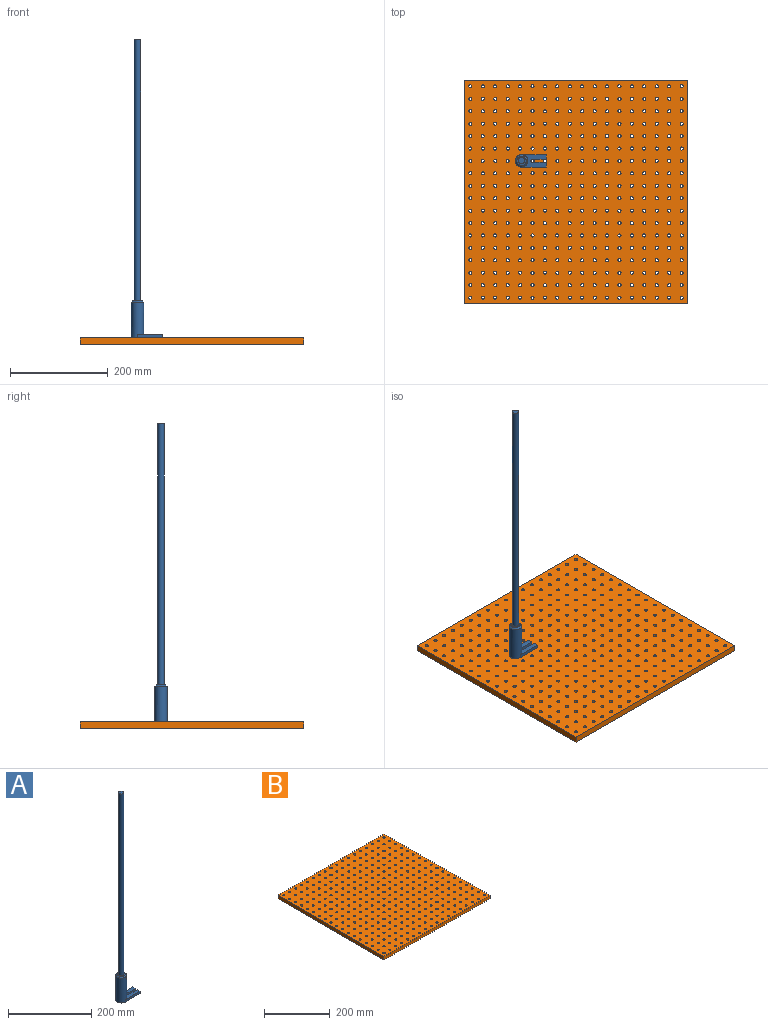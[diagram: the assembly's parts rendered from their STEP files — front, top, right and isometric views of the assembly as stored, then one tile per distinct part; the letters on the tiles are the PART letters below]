
ASSEMBLY  parts=2 mates=1
PART A: 14 faces, bbox 63.8x25.4x609.6 mm
  f0: cylinder r=12.7mm len=73.03mm, axis (0,0,-1), area 5575.7mm2, adj f2,f3,f7,f8,f11
  f1: plane 19.05x19.05mm, normal (0,0,1), area 158.3mm2, adj f11,f12
  f2: plane 63.8x25.4mm, normal (0,0,-1), area 1351mm2, adj f0,f4,f5,f6,f7,f8,f9,f10
  f3: plane 51.1x25.4mm, normal (0,0,1), area 844.3mm2, adj f0,f4,f5,f6,f7,f8,f9,f10
  f4: cylinder r=3.17mm len=6.35mm, axis (0,0,-1), area 62.4mm2, adj f2,f3,f5,f10
  f5: plane 28.58x6.35mm, normal (0,1,0), area 181.5mm2, adj f2,f3,f4,f6
  f6: plane 9.53x6.35mm, normal (1,0,0), area 60.5mm2, adj f2,f3,f5,f7
  f7: plane 50.8x6.35mm, normal (0,-1,0), area 322.6mm2, adj f0,f2,f3,f6
  f8: plane 50.8x6.35mm, normal (0,1,0), area 322.6mm2, adj f0,f2,f3,f9
  f9: plane 9.53x6.35mm, normal (1,0,0), area 60.5mm2, adj f2,f3,f8,f10
  f10: plane 28.43x6.35mm, normal (0,-1,0), area 180.5mm2, adj f2,f3,f4,f9
  f11: cone r=9.53mm half-angle=45deg, axis (0,0,-1), area 313.5mm2, adj f0,f1
  f12: cylinder r=6.35mm len=533.4mm, axis (0,0,-1), area 21281.7mm2, adj f1,f13
  f13: plane 12.7x12.7mm, normal (0,0,1), area 126.7mm2, adj f12
PART B: 330 faces, bbox 457.2x457.2x12.7 mm
  f0: plane 457.2x12.7mm, normal (-1,0,0), area 5806.4mm2, adj f1,f326,f328,f329
  f1: plane 457.2x12.7mm, normal (0,-1,0), area 5806.4mm2, adj f0,f2,f328,f329
  f2: plane 457.2x12.7mm, normal (1,0,0), area 5806.4mm2, adj f1,f326,f328,f329
  f3: cylinder r=3.17mm len=12.7mm, axis (0,0,-1), area 253.4mm2, adj f328,f329
  f4: cylinder r=3.17mm len=12.7mm, axis (0,0,-1), area 253.4mm2, adj f328,f329
  f5: cylinder r=3.17mm len=12.7mm, axis (0,0,-1), area 253.4mm2, adj f328,f329
  f6: cylinder r=3.17mm len=12.7mm, axis (0,0,-1), area 253.4mm2, adj f328,f329
  f7: cylinder r=3.17mm len=12.7mm, axis (0,0,-1), area 253.4mm2, adj f328,f329
  f8: cylinder r=3.17mm len=12.7mm, axis (0,0,-1), area 253.4mm2, adj f328,f329
  f9: cylinder r=3.17mm len=12.7mm, axis (0,0,-1), area 253.4mm2, adj f328,f329
  f10: cylinder r=3.17mm len=12.7mm, axis (0,0,-1), area 253.4mm2, adj f328,f329
  f11: cylinder r=3.17mm len=12.7mm, axis (0,0,-1), area 253.4mm2, adj f328,f329
  f12: cylinder r=3.17mm len=12.7mm, axis (0,0,-1), area 253.4mm2, adj f328,f329
  f13: cylinder r=3.17mm len=12.7mm, axis (0,0,-1), area 253.4mm2, adj f328,f329
  f14: cylinder r=3.17mm len=12.7mm, axis (0,0,-1), area 253.4mm2, adj f328,f329
  f15: cylinder r=3.17mm len=12.7mm, axis (0,0,-1), area 253.4mm2, adj f328,f329
  f16: cylinder r=3.17mm len=12.7mm, axis (0,0,-1), area 253.4mm2, adj f328,f329
  f17: cylinder r=3.17mm len=12.7mm, axis (0,0,-1), area 253.4mm2, adj f328,f329
  f18: cylinder r=3.17mm len=12.7mm, axis (0,0,-1), area 253.4mm2, adj f328,f329
  f19: cylinder r=3.17mm len=12.7mm, axis (0,0,-1), area 253.4mm2, adj f328,f329
  f20: cylinder r=3.17mm len=12.7mm, axis (0,0,-1), area 253.4mm2, adj f328,f329
  f21: cylinder r=3.17mm len=12.7mm, axis (0,0,-1), area 253.4mm2, adj f328,f329
  f22: cylinder r=3.17mm len=12.7mm, axis (0,0,-1), area 253.4mm2, adj f328,f329
  f23: cylinder r=3.17mm len=12.7mm, axis (0,0,-1), area 253.4mm2, adj f328,f329
  f24: cylinder r=3.17mm len=12.7mm, axis (0,0,-1), area 253.4mm2, adj f328,f329
  f25: cylinder r=3.17mm len=12.7mm, axis (0,0,-1), area 253.4mm2, adj f328,f329
  f26: cylinder r=3.17mm len=12.7mm, axis (0,0,-1), area 253.4mm2, adj f328,f329
  f27: cylinder r=3.17mm len=12.7mm, axis (0,0,-1), area 253.4mm2, adj f328,f329
  f28: cylinder r=3.17mm len=12.7mm, axis (0,0,-1), area 253.4mm2, adj f328,f329
  f29: cylinder r=3.17mm len=12.7mm, axis (0,0,-1), area 253.4mm2, adj f328,f329
  f30: cylinder r=3.17mm len=12.7mm, axis (0,0,-1), area 253.4mm2, adj f328,f329
  f31: cylinder r=3.17mm len=12.7mm, axis (0,0,-1), area 253.4mm2, adj f328,f329
  f32: cylinder r=3.17mm len=12.7mm, axis (0,0,-1), area 253.4mm2, adj f328,f329
  f33: cylinder r=3.17mm len=12.7mm, axis (0,0,-1), area 253.4mm2, adj f328,f329
  f34: cylinder r=3.17mm len=12.7mm, axis (0,0,-1), area 253.4mm2, adj f328,f329
  f35: cylinder r=3.17mm len=12.7mm, axis (0,0,-1), area 253.4mm2, adj f328,f329
  f36: cylinder r=3.17mm len=12.7mm, axis (0,0,-1), area 253.4mm2, adj f328,f329
  f37: cylinder r=3.17mm len=12.7mm, axis (0,0,-1), area 253.4mm2, adj f328,f329
  f38: cylinder r=3.17mm len=12.7mm, axis (0,0,-1), area 253.4mm2, adj f328,f329
  f39: cylinder r=3.17mm len=12.7mm, axis (0,0,-1), area 253.4mm2, adj f328,f329
  f40: cylinder r=3.17mm len=12.7mm, axis (0,0,-1), area 253.4mm2, adj f328,f329
  f41: cylinder r=3.17mm len=12.7mm, axis (0,0,-1), area 253.4mm2, adj f328,f329
  f42: cylinder r=3.17mm len=12.7mm, axis (0,0,-1), area 253.4mm2, adj f328,f329
  f43: cylinder r=3.17mm len=12.7mm, axis (0,0,-1), area 253.4mm2, adj f328,f329
  f44: cylinder r=3.17mm len=12.7mm, axis (0,0,-1), area 253.4mm2, adj f328,f329
  f45: cylinder r=3.17mm len=12.7mm, axis (0,0,-1), area 253.4mm2, adj f328,f329
  f46: cylinder r=3.17mm len=12.7mm, axis (0,0,-1), area 253.4mm2, adj f328,f329
  f47: cylinder r=3.17mm len=12.7mm, axis (0,0,-1), area 253.4mm2, adj f328,f329
  f48: cylinder r=3.17mm len=12.7mm, axis (0,0,-1), area 253.4mm2, adj f328,f329
  f49: cylinder r=3.17mm len=12.7mm, axis (0,0,-1), area 253.4mm2, adj f328,f329
  f50: cylinder r=3.17mm len=12.7mm, axis (0,0,-1), area 253.4mm2, adj f328,f329
  f51: cylinder r=3.17mm len=12.7mm, axis (0,0,-1), area 253.4mm2, adj f328,f329
  f52: cylinder r=3.17mm len=12.7mm, axis (0,0,-1), area 253.4mm2, adj f328,f329
  f53: cylinder r=3.17mm len=12.7mm, axis (0,0,-1), area 253.4mm2, adj f328,f329
  f54: cylinder r=3.17mm len=12.7mm, axis (0,0,-1), area 253.4mm2, adj f328,f329
  f55: cylinder r=3.17mm len=12.7mm, axis (0,0,-1), area 253.4mm2, adj f328,f329
  f56: cylinder r=3.17mm len=12.7mm, axis (0,0,-1), area 253.4mm2, adj f328,f329
  f57: cylinder r=3.17mm len=12.7mm, axis (0,0,-1), area 253.4mm2, adj f328,f329
  f58: cylinder r=3.17mm len=12.7mm, axis (0,0,-1), area 253.4mm2, adj f328,f329
  f59: cylinder r=3.17mm len=12.7mm, axis (0,0,-1), area 253.4mm2, adj f328,f329
  f60: cylinder r=3.17mm len=12.7mm, axis (0,0,-1), area 253.4mm2, adj f328,f329
  f61: cylinder r=3.17mm len=12.7mm, axis (0,0,-1), area 253.4mm2, adj f328,f329
  f62: cylinder r=3.17mm len=12.7mm, axis (0,0,-1), area 253.4mm2, adj f328,f329
  f63: cylinder r=3.17mm len=12.7mm, axis (0,0,-1), area 253.4mm2, adj f328,f329
  f64: cylinder r=3.17mm len=12.7mm, axis (0,0,-1), area 253.4mm2, adj f328,f329
  f65: cylinder r=3.17mm len=12.7mm, axis (0,0,-1), area 253.4mm2, adj f328,f329
  f66: cylinder r=3.17mm len=12.7mm, axis (0,0,-1), area 253.4mm2, adj f328,f329
  f67: cylinder r=3.17mm len=12.7mm, axis (0,0,-1), area 253.4mm2, adj f328,f329
  f68: cylinder r=3.17mm len=12.7mm, axis (0,0,-1), area 253.4mm2, adj f328,f329
  f69: cylinder r=3.17mm len=12.7mm, axis (0,0,-1), area 253.4mm2, adj f328,f329
  f70: cylinder r=3.17mm len=12.7mm, axis (0,0,-1), area 253.4mm2, adj f328,f329
  f71: cylinder r=3.17mm len=12.7mm, axis (0,0,-1), area 253.4mm2, adj f328,f329
  f72: cylinder r=3.17mm len=12.7mm, axis (0,0,-1), area 253.4mm2, adj f328,f329
  f73: cylinder r=3.17mm len=12.7mm, axis (0,0,-1), area 253.4mm2, adj f328,f329
  f74: cylinder r=3.17mm len=12.7mm, axis (0,0,-1), area 253.4mm2, adj f328,f329
  f75: cylinder r=3.17mm len=12.7mm, axis (0,0,-1), area 253.4mm2, adj f328,f329
  f76: cylinder r=3.17mm len=12.7mm, axis (0,0,-1), area 253.4mm2, adj f328,f329
  f77: cylinder r=3.17mm len=12.7mm, axis (0,0,-1), area 253.4mm2, adj f328,f329
  f78: cylinder r=3.17mm len=12.7mm, axis (0,0,-1), area 253.4mm2, adj f328,f329
  f79: cylinder r=3.17mm len=12.7mm, axis (0,0,-1), area 253.4mm2, adj f328,f329
  f80: cylinder r=3.17mm len=12.7mm, axis (0,0,-1), area 253.4mm2, adj f328,f329
  f81: cylinder r=3.17mm len=12.7mm, axis (0,0,-1), area 253.4mm2, adj f328,f329
  f82: cylinder r=3.17mm len=12.7mm, axis (0,0,-1), area 253.4mm2, adj f328,f329
  f83: cylinder r=3.17mm len=12.7mm, axis (0,0,-1), area 253.4mm2, adj f328,f329
  f84: cylinder r=3.17mm len=12.7mm, axis (0,0,-1), area 253.4mm2, adj f328,f329
  f85: cylinder r=3.17mm len=12.7mm, axis (0,0,-1), area 253.4mm2, adj f328,f329
  f86: cylinder r=3.17mm len=12.7mm, axis (0,0,-1), area 253.4mm2, adj f328,f329
  f87: cylinder r=3.17mm len=12.7mm, axis (0,0,-1), area 253.4mm2, adj f328,f329
  f88: cylinder r=3.17mm len=12.7mm, axis (0,0,-1), area 253.4mm2, adj f328,f329
  f89: cylinder r=3.17mm len=12.7mm, axis (0,0,-1), area 253.4mm2, adj f328,f329
  f90: cylinder r=3.17mm len=12.7mm, axis (0,0,-1), area 253.4mm2, adj f328,f329
  f91: cylinder r=3.17mm len=12.7mm, axis (0,0,-1), area 253.4mm2, adj f328,f329
  f92: cylinder r=3.17mm len=12.7mm, axis (0,0,-1), area 253.4mm2, adj f328,f329
  f93: cylinder r=3.17mm len=12.7mm, axis (0,0,-1), area 253.4mm2, adj f328,f329
  f94: cylinder r=3.17mm len=12.7mm, axis (0,0,-1), area 253.4mm2, adj f328,f329
  f95: cylinder r=3.17mm len=12.7mm, axis (0,0,-1), area 253.4mm2, adj f328,f329
  f96: cylinder r=3.17mm len=12.7mm, axis (0,0,-1), area 253.4mm2, adj f328,f329
  f97: cylinder r=3.17mm len=12.7mm, axis (0,0,-1), area 253.4mm2, adj f328,f329
  f98: cylinder r=3.17mm len=12.7mm, axis (0,0,-1), area 253.4mm2, adj f328,f329
  f99: cylinder r=3.17mm len=12.7mm, axis (0,0,-1), area 253.4mm2, adj f328,f329
  f100: cylinder r=3.17mm len=12.7mm, axis (0,0,-1), area 253.4mm2, adj f328,f329
  f101: cylinder r=3.17mm len=12.7mm, axis (0,0,-1), area 253.4mm2, adj f328,f329
  f102: cylinder r=3.17mm len=12.7mm, axis (0,0,-1), area 253.4mm2, adj f328,f329
  f103: cylinder r=3.17mm len=12.7mm, axis (0,0,-1), area 253.4mm2, adj f328,f329
  f104: cylinder r=3.17mm len=12.7mm, axis (0,0,-1), area 253.4mm2, adj f328,f329
  f105: cylinder r=3.17mm len=12.7mm, axis (0,0,-1), area 253.4mm2, adj f328,f329
  f106: cylinder r=3.17mm len=12.7mm, axis (0,0,-1), area 253.4mm2, adj f328,f329
  f107: cylinder r=3.17mm len=12.7mm, axis (0,0,-1), area 253.4mm2, adj f328,f329
  f108: cylinder r=3.17mm len=12.7mm, axis (0,0,-1), area 253.4mm2, adj f328,f329
  f109: cylinder r=3.17mm len=12.7mm, axis (0,0,-1), area 253.4mm2, adj f328,f329
  f110: cylinder r=3.17mm len=12.7mm, axis (0,0,-1), area 253.4mm2, adj f328,f329
  f111: cylinder r=3.17mm len=12.7mm, axis (0,0,-1), area 253.4mm2, adj f328,f329
  f112: cylinder r=3.17mm len=12.7mm, axis (0,0,-1), area 253.4mm2, adj f328,f329
  f113: cylinder r=3.17mm len=12.7mm, axis (0,0,-1), area 253.4mm2, adj f328,f329
  f114: cylinder r=3.17mm len=12.7mm, axis (0,0,-1), area 253.4mm2, adj f328,f329
  f115: cylinder r=3.17mm len=12.7mm, axis (0,0,-1), area 253.4mm2, adj f328,f329
  f116: cylinder r=3.17mm len=12.7mm, axis (0,0,-1), area 253.4mm2, adj f328,f329
  f117: cylinder r=3.17mm len=12.7mm, axis (0,0,-1), area 253.4mm2, adj f328,f329
  f118: cylinder r=3.17mm len=12.7mm, axis (0,0,-1), area 253.4mm2, adj f328,f329
  f119: cylinder r=3.17mm len=12.7mm, axis (0,0,-1), area 253.4mm2, adj f328,f329
  f120: cylinder r=3.17mm len=12.7mm, axis (0,0,-1), area 253.4mm2, adj f328,f329
  f121: cylinder r=3.17mm len=12.7mm, axis (0,0,-1), area 253.4mm2, adj f328,f329
  f122: cylinder r=3.17mm len=12.7mm, axis (0,0,-1), area 253.4mm2, adj f328,f329
  f123: cylinder r=3.17mm len=12.7mm, axis (0,0,-1), area 253.4mm2, adj f328,f329
  f124: cylinder r=3.17mm len=12.7mm, axis (0,0,-1), area 253.4mm2, adj f328,f329
  f125: cylinder r=3.17mm len=12.7mm, axis (0,0,-1), area 253.4mm2, adj f328,f329
  f126: cylinder r=3.17mm len=12.7mm, axis (0,0,-1), area 253.4mm2, adj f328,f329
  f127: cylinder r=3.17mm len=12.7mm, axis (0,0,-1), area 253.4mm2, adj f328,f329
  f128: cylinder r=3.17mm len=12.7mm, axis (0,0,-1), area 253.4mm2, adj f328,f329
  f129: cylinder r=3.17mm len=12.7mm, axis (0,0,-1), area 253.4mm2, adj f328,f329
  f130: cylinder r=3.17mm len=12.7mm, axis (0,0,-1), area 253.4mm2, adj f328,f329
  f131: cylinder r=3.17mm len=12.7mm, axis (0,0,-1), area 253.4mm2, adj f328,f329
  f132: cylinder r=3.17mm len=12.7mm, axis (0,0,-1), area 253.4mm2, adj f328,f329
  f133: cylinder r=3.17mm len=12.7mm, axis (0,0,-1), area 253.4mm2, adj f328,f329
  f134: cylinder r=3.17mm len=12.7mm, axis (0,0,-1), area 253.4mm2, adj f328,f329
  f135: cylinder r=3.17mm len=12.7mm, axis (0,0,-1), area 253.4mm2, adj f328,f329
  f136: cylinder r=3.17mm len=12.7mm, axis (0,0,-1), area 253.4mm2, adj f328,f329
  f137: cylinder r=3.17mm len=12.7mm, axis (0,0,-1), area 253.4mm2, adj f328,f329
  f138: cylinder r=3.17mm len=12.7mm, axis (0,0,-1), area 253.4mm2, adj f328,f329
  f139: cylinder r=3.17mm len=12.7mm, axis (0,0,-1), area 253.4mm2, adj f328,f329
  f140: cylinder r=3.17mm len=12.7mm, axis (0,0,-1), area 253.4mm2, adj f328,f329
  f141: cylinder r=3.17mm len=12.7mm, axis (0,0,-1), area 253.4mm2, adj f328,f329
  f142: cylinder r=3.17mm len=12.7mm, axis (0,0,-1), area 253.4mm2, adj f328,f329
  f143: cylinder r=3.17mm len=12.7mm, axis (0,0,-1), area 253.4mm2, adj f328,f329
  f144: cylinder r=3.17mm len=12.7mm, axis (0,0,-1), area 253.4mm2, adj f328,f329
  f145: cylinder r=3.17mm len=12.7mm, axis (0,0,-1), area 253.4mm2, adj f328,f329
  f146: cylinder r=3.17mm len=12.7mm, axis (0,0,-1), area 253.4mm2, adj f328,f329
  f147: cylinder r=3.17mm len=12.7mm, axis (0,0,-1), area 253.4mm2, adj f328,f329
  f148: cylinder r=3.17mm len=12.7mm, axis (0,0,-1), area 253.4mm2, adj f328,f329
  f149: cylinder r=3.17mm len=12.7mm, axis (0,0,-1), area 253.4mm2, adj f328,f329
  f150: cylinder r=3.17mm len=12.7mm, axis (0,0,-1), area 253.4mm2, adj f328,f329
  f151: cylinder r=3.17mm len=12.7mm, axis (0,0,-1), area 253.4mm2, adj f328,f329
  f152: cylinder r=3.17mm len=12.7mm, axis (0,0,-1), area 253.4mm2, adj f328,f329
  f153: cylinder r=3.17mm len=12.7mm, axis (0,0,-1), area 253.4mm2, adj f328,f329
  f154: cylinder r=3.17mm len=12.7mm, axis (0,0,-1), area 253.4mm2, adj f328,f329
  f155: cylinder r=3.17mm len=12.7mm, axis (0,0,-1), area 253.4mm2, adj f328,f329
  f156: cylinder r=3.17mm len=12.7mm, axis (0,0,-1), area 253.4mm2, adj f328,f329
  f157: cylinder r=3.17mm len=12.7mm, axis (0,0,-1), area 253.4mm2, adj f328,f329
  f158: cylinder r=3.17mm len=12.7mm, axis (0,0,-1), area 253.4mm2, adj f328,f329
  f159: cylinder r=3.17mm len=12.7mm, axis (0,0,-1), area 253.4mm2, adj f328,f329
  f160: cylinder r=3.17mm len=12.7mm, axis (0,0,-1), area 253.4mm2, adj f328,f329
  f161: cylinder r=3.17mm len=12.7mm, axis (0,0,-1), area 253.4mm2, adj f328,f329
  f162: cylinder r=3.17mm len=12.7mm, axis (0,0,-1), area 253.4mm2, adj f328,f329
  f163: cylinder r=3.17mm len=12.7mm, axis (0,0,-1), area 253.4mm2, adj f328,f329
  f164: cylinder r=3.17mm len=12.7mm, axis (0,0,-1), area 253.4mm2, adj f328,f329
  f165: cylinder r=3.17mm len=12.7mm, axis (0,0,-1), area 253.4mm2, adj f328,f329
  f166: cylinder r=3.17mm len=12.7mm, axis (0,0,-1), area 253.4mm2, adj f328,f329
  f167: cylinder r=3.17mm len=12.7mm, axis (0,0,-1), area 253.4mm2, adj f328,f329
  f168: cylinder r=3.17mm len=12.7mm, axis (0,0,-1), area 253.4mm2, adj f328,f329
  f169: cylinder r=3.17mm len=12.7mm, axis (0,0,-1), area 253.4mm2, adj f328,f329
  f170: cylinder r=3.17mm len=12.7mm, axis (0,0,-1), area 253.4mm2, adj f328,f329
  f171: cylinder r=3.17mm len=12.7mm, axis (0,0,-1), area 253.4mm2, adj f328,f329
  f172: cylinder r=3.17mm len=12.7mm, axis (0,0,-1), area 253.4mm2, adj f328,f329
  f173: cylinder r=3.17mm len=12.7mm, axis (0,0,-1), area 253.4mm2, adj f328,f329
  f174: cylinder r=3.17mm len=12.7mm, axis (0,0,-1), area 253.4mm2, adj f328,f329
  f175: cylinder r=3.17mm len=12.7mm, axis (0,0,-1), area 253.4mm2, adj f328,f329
  f176: cylinder r=3.17mm len=12.7mm, axis (0,0,-1), area 253.4mm2, adj f328,f329
  f177: cylinder r=3.17mm len=12.7mm, axis (0,0,-1), area 253.4mm2, adj f328,f329
  f178: cylinder r=3.17mm len=12.7mm, axis (0,0,-1), area 253.4mm2, adj f328,f329
  f179: cylinder r=3.17mm len=12.7mm, axis (0,0,-1), area 253.4mm2, adj f328,f329
  f180: cylinder r=3.17mm len=12.7mm, axis (0,0,-1), area 253.4mm2, adj f328,f329
  f181: cylinder r=3.17mm len=12.7mm, axis (0,0,-1), area 253.4mm2, adj f328,f329
  f182: cylinder r=3.17mm len=12.7mm, axis (0,0,-1), area 253.4mm2, adj f328,f329
  f183: cylinder r=3.17mm len=12.7mm, axis (0,0,-1), area 253.4mm2, adj f328,f329
  f184: cylinder r=3.17mm len=12.7mm, axis (0,0,-1), area 253.4mm2, adj f328,f329
  f185: cylinder r=3.17mm len=12.7mm, axis (0,0,-1), area 253.4mm2, adj f328,f329
  f186: cylinder r=3.17mm len=12.7mm, axis (0,0,-1), area 253.4mm2, adj f328,f329
  f187: cylinder r=3.17mm len=12.7mm, axis (0,0,-1), area 253.4mm2, adj f328,f329
  f188: cylinder r=3.17mm len=12.7mm, axis (0,0,-1), area 253.4mm2, adj f328,f329
  f189: cylinder r=3.17mm len=12.7mm, axis (0,0,-1), area 253.4mm2, adj f328,f329
  f190: cylinder r=3.17mm len=12.7mm, axis (0,0,-1), area 253.4mm2, adj f328,f329
  f191: cylinder r=3.17mm len=12.7mm, axis (0,0,-1), area 253.4mm2, adj f328,f329
  f192: cylinder r=3.17mm len=12.7mm, axis (0,0,-1), area 253.4mm2, adj f328,f329
  f193: cylinder r=3.17mm len=12.7mm, axis (0,0,-1), area 253.4mm2, adj f328,f329
  f194: cylinder r=3.17mm len=12.7mm, axis (0,0,-1), area 253.4mm2, adj f328,f329
  f195: cylinder r=3.17mm len=12.7mm, axis (0,0,-1), area 253.4mm2, adj f328,f329
  f196: cylinder r=3.17mm len=12.7mm, axis (0,0,-1), area 253.4mm2, adj f328,f329
  f197: cylinder r=3.17mm len=12.7mm, axis (0,0,-1), area 253.4mm2, adj f328,f329
  f198: cylinder r=3.17mm len=12.7mm, axis (0,0,-1), area 253.4mm2, adj f328,f329
  f199: cylinder r=3.17mm len=12.7mm, axis (0,0,-1), area 253.4mm2, adj f328,f329
  f200: cylinder r=3.17mm len=12.7mm, axis (0,0,-1), area 253.4mm2, adj f328,f329
  f201: cylinder r=3.17mm len=12.7mm, axis (0,0,-1), area 253.4mm2, adj f328,f329
  f202: cylinder r=3.17mm len=12.7mm, axis (0,0,-1), area 253.4mm2, adj f328,f329
  f203: cylinder r=3.17mm len=12.7mm, axis (0,0,-1), area 253.4mm2, adj f328,f329
  f204: cylinder r=3.17mm len=12.7mm, axis (0,0,-1), area 253.4mm2, adj f328,f329
  f205: cylinder r=3.17mm len=12.7mm, axis (0,0,-1), area 253.4mm2, adj f328,f329
  f206: cylinder r=3.17mm len=12.7mm, axis (0,0,-1), area 253.4mm2, adj f328,f329
  f207: cylinder r=3.17mm len=12.7mm, axis (0,0,-1), area 253.4mm2, adj f328,f329
  f208: cylinder r=3.17mm len=12.7mm, axis (0,0,-1), area 253.4mm2, adj f328,f329
  f209: cylinder r=3.17mm len=12.7mm, axis (0,0,-1), area 253.4mm2, adj f328,f329
  f210: cylinder r=3.17mm len=12.7mm, axis (0,0,-1), area 253.4mm2, adj f328,f329
  f211: cylinder r=3.17mm len=12.7mm, axis (0,0,-1), area 253.4mm2, adj f328,f329
  f212: cylinder r=3.17mm len=12.7mm, axis (0,0,-1), area 253.4mm2, adj f328,f329
  f213: cylinder r=3.17mm len=12.7mm, axis (0,0,-1), area 253.4mm2, adj f328,f329
  f214: cylinder r=3.17mm len=12.7mm, axis (0,0,-1), area 253.4mm2, adj f328,f329
  f215: cylinder r=3.17mm len=12.7mm, axis (0,0,-1), area 253.4mm2, adj f328,f329
  f216: cylinder r=3.17mm len=12.7mm, axis (0,0,-1), area 253.4mm2, adj f328,f329
  f217: cylinder r=3.17mm len=12.7mm, axis (0,0,-1), area 253.4mm2, adj f328,f329
  f218: cylinder r=3.17mm len=12.7mm, axis (0,0,-1), area 253.4mm2, adj f328,f329
  f219: cylinder r=3.17mm len=12.7mm, axis (0,0,-1), area 253.4mm2, adj f328,f329
  f220: cylinder r=3.17mm len=12.7mm, axis (0,0,-1), area 253.4mm2, adj f328,f329
  f221: cylinder r=3.17mm len=12.7mm, axis (0,0,-1), area 253.4mm2, adj f328,f329
  f222: cylinder r=3.17mm len=12.7mm, axis (0,0,-1), area 253.4mm2, adj f328,f329
  f223: cylinder r=3.17mm len=12.7mm, axis (0,0,-1), area 253.4mm2, adj f328,f329
  f224: cylinder r=3.17mm len=12.7mm, axis (0,0,-1), area 253.4mm2, adj f328,f329
  f225: cylinder r=3.17mm len=12.7mm, axis (0,0,-1), area 253.4mm2, adj f328,f329
  f226: cylinder r=3.17mm len=12.7mm, axis (0,0,-1), area 253.4mm2, adj f328,f329
  f227: cylinder r=3.17mm len=12.7mm, axis (0,0,-1), area 253.4mm2, adj f328,f329
  f228: cylinder r=3.17mm len=12.7mm, axis (0,0,-1), area 253.4mm2, adj f328,f329
  f229: cylinder r=3.17mm len=12.7mm, axis (0,0,-1), area 253.4mm2, adj f328,f329
  f230: cylinder r=3.17mm len=12.7mm, axis (0,0,-1), area 253.4mm2, adj f328,f329
  f231: cylinder r=3.17mm len=12.7mm, axis (0,0,-1), area 253.4mm2, adj f328,f329
  f232: cylinder r=3.17mm len=12.7mm, axis (0,0,-1), area 253.4mm2, adj f328,f329
  f233: cylinder r=3.17mm len=12.7mm, axis (0,0,-1), area 253.4mm2, adj f328,f329
  f234: cylinder r=3.17mm len=12.7mm, axis (0,0,-1), area 253.4mm2, adj f328,f329
  f235: cylinder r=3.17mm len=12.7mm, axis (0,0,-1), area 253.4mm2, adj f328,f329
  f236: cylinder r=3.17mm len=12.7mm, axis (0,0,-1), area 253.4mm2, adj f328,f329
  f237: cylinder r=3.17mm len=12.7mm, axis (0,0,-1), area 253.4mm2, adj f328,f329
  f238: cylinder r=3.17mm len=12.7mm, axis (0,0,-1), area 253.4mm2, adj f328,f329
  f239: cylinder r=3.17mm len=12.7mm, axis (0,0,-1), area 253.4mm2, adj f328,f329
  f240: cylinder r=3.17mm len=12.7mm, axis (0,0,-1), area 253.4mm2, adj f328,f329
  f241: cylinder r=3.17mm len=12.7mm, axis (0,0,-1), area 253.4mm2, adj f328,f329
  f242: cylinder r=3.17mm len=12.7mm, axis (0,0,-1), area 253.4mm2, adj f328,f329
  f243: cylinder r=3.17mm len=12.7mm, axis (0,0,-1), area 253.4mm2, adj f328,f329
  f244: cylinder r=3.17mm len=12.7mm, axis (0,0,-1), area 253.4mm2, adj f328,f329
  f245: cylinder r=3.17mm len=12.7mm, axis (0,0,-1), area 253.4mm2, adj f328,f329
  f246: cylinder r=3.17mm len=12.7mm, axis (0,0,-1), area 253.4mm2, adj f328,f329
  f247: cylinder r=3.17mm len=12.7mm, axis (0,0,-1), area 253.4mm2, adj f328,f329
  f248: cylinder r=3.17mm len=12.7mm, axis (0,0,-1), area 253.4mm2, adj f328,f329
  f249: cylinder r=3.17mm len=12.7mm, axis (0,0,-1), area 253.4mm2, adj f328,f329
  f250: cylinder r=3.17mm len=12.7mm, axis (0,0,-1), area 253.4mm2, adj f328,f329
  f251: cylinder r=3.17mm len=12.7mm, axis (0,0,-1), area 253.4mm2, adj f328,f329
  f252: cylinder r=3.17mm len=12.7mm, axis (0,0,-1), area 253.4mm2, adj f328,f329
  f253: cylinder r=3.17mm len=12.7mm, axis (0,0,-1), area 253.4mm2, adj f328,f329
  f254: cylinder r=3.17mm len=12.7mm, axis (0,0,-1), area 253.4mm2, adj f328,f329
  f255: cylinder r=3.17mm len=12.7mm, axis (0,0,-1), area 253.4mm2, adj f328,f329
  f256: cylinder r=3.17mm len=12.7mm, axis (0,0,-1), area 253.4mm2, adj f328,f329
  f257: cylinder r=3.17mm len=12.7mm, axis (0,0,-1), area 253.4mm2, adj f328,f329
  f258: cylinder r=3.17mm len=12.7mm, axis (0,0,-1), area 253.4mm2, adj f328,f329
  f259: cylinder r=3.17mm len=12.7mm, axis (0,0,-1), area 253.4mm2, adj f328,f329
  f260: cylinder r=3.17mm len=12.7mm, axis (0,0,-1), area 253.4mm2, adj f328,f329
  f261: cylinder r=3.17mm len=12.7mm, axis (0,0,-1), area 253.4mm2, adj f328,f329
  f262: cylinder r=3.17mm len=12.7mm, axis (0,0,-1), area 253.4mm2, adj f328,f329
  f263: cylinder r=3.17mm len=12.7mm, axis (0,0,-1), area 253.4mm2, adj f328,f329
  f264: cylinder r=3.17mm len=12.7mm, axis (0,0,-1), area 253.4mm2, adj f328,f329
  f265: cylinder r=3.17mm len=12.7mm, axis (0,0,-1), area 253.4mm2, adj f328,f329
  f266: cylinder r=3.17mm len=12.7mm, axis (0,0,-1), area 253.4mm2, adj f328,f329
  f267: cylinder r=3.17mm len=12.7mm, axis (0,0,-1), area 253.4mm2, adj f328,f329
  f268: cylinder r=3.17mm len=12.7mm, axis (0,0,-1), area 253.4mm2, adj f328,f329
  f269: cylinder r=3.17mm len=12.7mm, axis (0,0,-1), area 253.4mm2, adj f328,f329
  f270: cylinder r=3.17mm len=12.7mm, axis (0,0,-1), area 253.4mm2, adj f328,f329
  f271: cylinder r=3.17mm len=12.7mm, axis (0,0,-1), area 253.4mm2, adj f328,f329
  f272: cylinder r=3.17mm len=12.7mm, axis (0,0,-1), area 253.4mm2, adj f328,f329
  f273: cylinder r=3.17mm len=12.7mm, axis (0,0,-1), area 253.4mm2, adj f328,f329
  f274: cylinder r=3.17mm len=12.7mm, axis (0,0,-1), area 253.4mm2, adj f328,f329
  f275: cylinder r=3.17mm len=12.7mm, axis (0,0,-1), area 253.4mm2, adj f328,f329
  f276: cylinder r=3.17mm len=12.7mm, axis (0,0,-1), area 253.4mm2, adj f328,f329
  f277: cylinder r=3.17mm len=12.7mm, axis (0,0,-1), area 253.4mm2, adj f328,f329
  f278: cylinder r=3.17mm len=12.7mm, axis (0,0,-1), area 253.4mm2, adj f328,f329
  f279: cylinder r=3.17mm len=12.7mm, axis (0,0,-1), area 253.4mm2, adj f328,f329
  f280: cylinder r=3.17mm len=12.7mm, axis (0,0,-1), area 253.4mm2, adj f328,f329
  f281: cylinder r=3.17mm len=12.7mm, axis (0,0,-1), area 253.4mm2, adj f328,f329
  f282: cylinder r=3.17mm len=12.7mm, axis (0,0,-1), area 253.4mm2, adj f328,f329
  f283: cylinder r=3.17mm len=12.7mm, axis (0,0,-1), area 253.4mm2, adj f328,f329
  f284: cylinder r=3.17mm len=12.7mm, axis (0,0,-1), area 253.4mm2, adj f328,f329
  f285: cylinder r=3.17mm len=12.7mm, axis (0,0,-1), area 253.4mm2, adj f328,f329
  f286: cylinder r=3.17mm len=12.7mm, axis (0,0,-1), area 253.4mm2, adj f328,f329
  f287: cylinder r=3.17mm len=12.7mm, axis (0,0,-1), area 253.4mm2, adj f328,f329
  f288: cylinder r=3.17mm len=12.7mm, axis (0,0,-1), area 253.4mm2, adj f328,f329
  f289: cylinder r=3.17mm len=12.7mm, axis (0,0,-1), area 253.4mm2, adj f328,f329
  f290: cylinder r=3.17mm len=12.7mm, axis (0,0,-1), area 253.4mm2, adj f328,f329
  f291: cylinder r=3.17mm len=12.7mm, axis (0,0,-1), area 253.4mm2, adj f328,f329
  f292: cylinder r=3.17mm len=12.7mm, axis (0,0,-1), area 253.4mm2, adj f328,f329
  f293: cylinder r=3.17mm len=12.7mm, axis (0,0,-1), area 253.4mm2, adj f328,f329
  f294: cylinder r=3.17mm len=12.7mm, axis (0,0,-1), area 253.4mm2, adj f328,f329
  f295: cylinder r=3.17mm len=12.7mm, axis (0,0,-1), area 253.4mm2, adj f328,f329
  f296: cylinder r=3.17mm len=12.7mm, axis (0,0,-1), area 253.4mm2, adj f328,f329
  f297: cylinder r=3.17mm len=12.7mm, axis (0,0,-1), area 253.4mm2, adj f328,f329
  f298: cylinder r=3.17mm len=12.7mm, axis (0,0,-1), area 253.4mm2, adj f328,f329
  f299: cylinder r=3.17mm len=12.7mm, axis (0,0,-1), area 253.4mm2, adj f328,f329
  f300: cylinder r=3.17mm len=12.7mm, axis (0,0,-1), area 253.4mm2, adj f328,f329
  f301: cylinder r=3.17mm len=12.7mm, axis (0,0,-1), area 253.4mm2, adj f328,f329
  f302: cylinder r=3.17mm len=12.7mm, axis (0,0,-1), area 253.4mm2, adj f328,f329
  f303: cylinder r=3.17mm len=12.7mm, axis (0,0,-1), area 253.4mm2, adj f328,f329
  f304: cylinder r=3.17mm len=12.7mm, axis (0,0,-1), area 253.4mm2, adj f328,f329
  f305: cylinder r=3.17mm len=12.7mm, axis (0,0,-1), area 253.4mm2, adj f328,f329
  f306: cylinder r=3.17mm len=12.7mm, axis (0,0,-1), area 253.4mm2, adj f328,f329
  f307: cylinder r=3.17mm len=12.7mm, axis (0,0,-1), area 253.4mm2, adj f328,f329
  f308: cylinder r=3.17mm len=12.7mm, axis (0,0,-1), area 253.4mm2, adj f328,f329
  f309: cylinder r=3.17mm len=12.7mm, axis (0,0,-1), area 253.4mm2, adj f328,f329
  f310: cylinder r=3.17mm len=12.7mm, axis (0,0,-1), area 253.4mm2, adj f328,f329
  f311: cylinder r=3.17mm len=12.7mm, axis (0,0,-1), area 253.4mm2, adj f328,f329
  f312: cylinder r=3.17mm len=12.7mm, axis (0,0,-1), area 253.4mm2, adj f328,f329
  f313: cylinder r=3.17mm len=12.7mm, axis (0,0,-1), area 253.4mm2, adj f328,f329
  f314: cylinder r=3.17mm len=12.7mm, axis (0,0,-1), area 253.4mm2, adj f328,f329
  f315: cylinder r=3.17mm len=12.7mm, axis (0,0,-1), area 253.4mm2, adj f328,f329
  f316: cylinder r=3.17mm len=12.7mm, axis (0,0,-1), area 253.4mm2, adj f328,f329
  f317: cylinder r=3.17mm len=12.7mm, axis (0,0,-1), area 253.4mm2, adj f328,f329
  f318: cylinder r=3.17mm len=12.7mm, axis (0,0,-1), area 253.4mm2, adj f328,f329
  f319: cylinder r=3.17mm len=12.7mm, axis (0,0,-1), area 253.4mm2, adj f328,f329
  f320: cylinder r=3.17mm len=12.7mm, axis (0,0,-1), area 253.4mm2, adj f328,f329
  f321: cylinder r=3.17mm len=12.7mm, axis (0,0,-1), area 253.4mm2, adj f328,f329
  f322: cylinder r=3.17mm len=12.7mm, axis (0,0,-1), area 253.4mm2, adj f328,f329
  f323: cylinder r=3.17mm len=12.7mm, axis (0,0,-1), area 253.4mm2, adj f328,f329
  f324: cylinder r=3.17mm len=12.7mm, axis (0,0,-1), area 253.4mm2, adj f328,f329
  f325: cylinder r=3.17mm len=12.7mm, axis (0,0,-1), area 253.4mm2, adj f328,f329
  f326: plane 457.2x12.7mm, normal (0,1,0), area 5806.4mm2, adj f0,f2,f328,f329
  f327: cylinder r=3.17mm len=12.7mm, axis (0,0,-1), area 253.4mm2, adj f328,f329
  f328: plane 457.2x457.2mm, normal (0,0,1), area 198771mm2, adj f0,f1,f2,f3,f4,f5,f6,f7
  f329: plane 457.2x457.2mm, normal (0,0,-1), area 198771mm2, adj f0,f1,f2,f3,f4,f5,f6,f7
PLACE A t=(-71.03,-1108.76,501)mm
PLACE B t=(65.62,-991.93,501)mm
MATE fastened B.f229 <-> A.f4  axis (0,0,1) through (205.32,-699.83,513.7)mm
